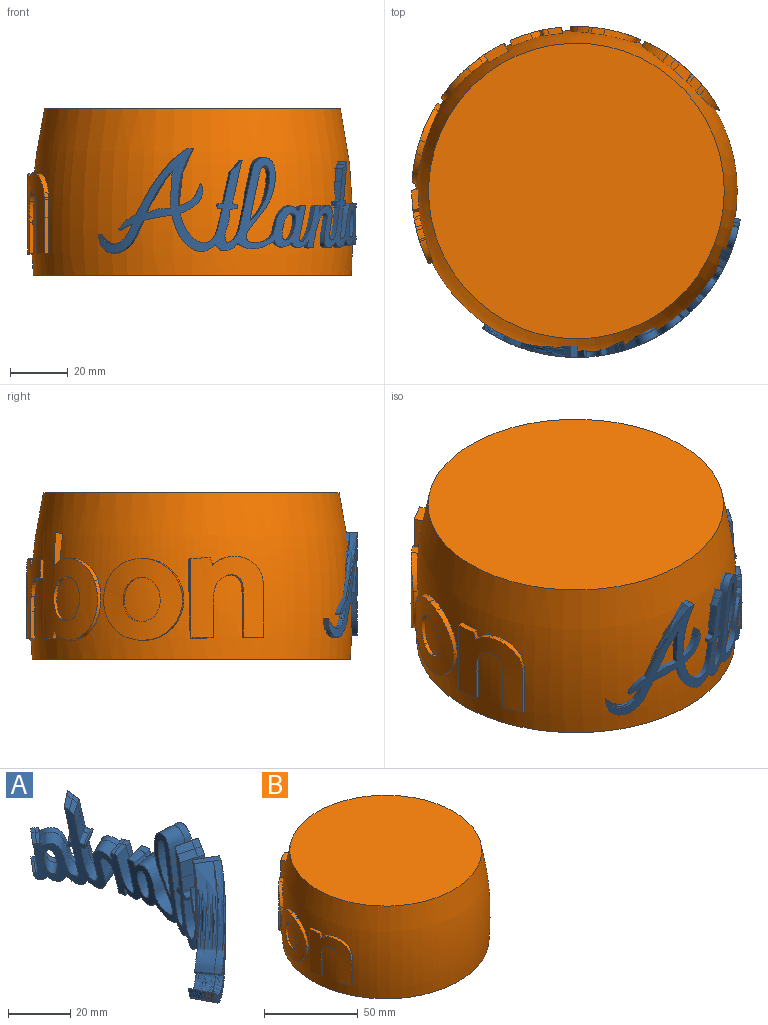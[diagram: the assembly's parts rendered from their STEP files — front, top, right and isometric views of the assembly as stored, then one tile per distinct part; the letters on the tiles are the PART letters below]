
ASSEMBLY  parts=2 mates=1
PART A: 143 faces, bbox 37x96.3x36.3 mm
  f0: bspline ~14.65x13.65mm, area 59.4mm2, adj f1,f70,f71,f133
  f1: bspline ~2.82x2.61mm, area 3.4mm2, adj f0,f2,f71,f132
  f2: bspline ~2.21x1.78mm, area 3.6mm2, adj f1,f3,f71,f131
  f3: bspline ~12.78x11.38mm, area 50.7mm2, adj f2,f4,f71,f130
  f4: bspline ~2.76x1.98mm, area 3.5mm2, adj f3,f5,f71,f129
  f5: bspline ~2.54x1.41mm, area 2mm2, adj f4,f6,f71,f128
  f6: bspline ~19.2x6.49mm, area 51.9mm2, adj f5,f7,f71,f127
  f7: bspline ~2.59x1.72mm, area 4.8mm2, adj f6,f8,f71,f126
  f8: bspline ~2.54x0.68mm, area 2.1mm2, adj f7,f9,f71,f125
  f9: bspline ~6.09x2.81mm, area 17mm2, adj f8,f10,f71,f124
  f10: bspline ~2.59x0.91mm, area 2.1mm2, adj f9,f11,f71,f123
  f11: bspline ~2.58x0.74mm, area 2mm2, adj f10,f12,f71,f122
  f12: bspline ~6.59x3.58mm, area 17.9mm2, adj f11,f13,f71,f121
  f13: bspline ~2.64x1.3mm, area 2.4mm2, adj f12,f14,f71,f120
  f14: bspline ~2.52x1.24mm, area 3.2mm2, adj f13,f15,f71,f119
  f15: bspline ~14.26x12.03mm, area 89.4mm2, adj f14,f16,f71,f118
  f16: bspline ~2.75x2.16mm, area 3.4mm2, adj f15,f17,f71,f117
  f17: bspline ~2.35x1.48mm, area 1.4mm2, adj f16,f18,f71,f116
  f18: bspline ~12.65x10.28mm, area 40.6mm2, adj f17,f19,f71,f115
  f19: bspline ~2.38x2.34mm, area 2.6mm2, adj f18,f20,f71,f114
  f20: bspline ~2.05x2.02mm, area 1.3mm2, adj f19,f21,f71,f113
  f21: bspline ~5.29x5.16mm, area 15.6mm2, adj f20,f22,f71,f112
  f22: bspline ~2.02x1.74mm, area 1.6mm2, adj f21,f23,f71,f111
  f23: bspline ~2.48x2.3mm, area 2.2mm2, adj f22,f24,f71,f110
  f24: bspline ~6.09x2.51mm, area 17.5mm2, adj f23,f25,f71,f109
  f25: bspline ~5.23x2.82mm, area 16.8mm2, adj f24,f26,f71,f108
  f26: bspline ~2.71x2.62mm, area 3.1mm2, adj f25,f27,f71,f107
  f27: bspline ~1.96x1.83mm, area 1.7mm2, adj f26,f28,f71,f106
  f28: bspline ~12.6x12.17mm, area 82.4mm2, adj f27,f29,f71,f105
  f29: bspline ~2.24x1.68mm, area 3.2mm2, adj f28,f30,f71,f104
  f30: bspline ~2.69x2.35mm, area 2.7mm2, adj f29,f31,f71,f103
  f31: bspline ~2.65x2.33mm, area 8.2mm2, adj f30,f32,f71,f102
  f32: bspline ~2.49x2.07mm, area 1.8mm2, adj f31,f33,f71,f101
  f33: bspline ~2.13x1.55mm, area 1.8mm2, adj f32,f34,f71,f100
  f34: bspline ~13.08x3.66mm, area 39.6mm2, adj f33,f35,f71,f99
  f35: bspline ~3.08x2.89mm, area 5.6mm2, adj f34,f36,f71,f98
  f36: bspline ~4.43x2.6mm, area 11.5mm2, adj f35,f37,f71,f97
  f37: bspline ~6.86x3.93mm, area 21.4mm2, adj f36,f38,f71,f96
  f38: bspline ~2.53x1.85mm, area 1.7mm2, adj f37,f39,f71,f95
  f39: bspline ~2.27x1.37mm, area 2mm2, adj f38,f40,f71,f94
  f40: bspline ~2.26x1.38mm, area 2mm2, adj f39,f41,f71,f93
  f41: bspline ~2.61x2.01mm, area 2.1mm2, adj f40,f42,f71,f92
  f42: bspline ~2.61x2.03mm, area 2.1mm2, adj f41,f43,f71,f91
  f43: bspline ~2.2x1.4mm, area 1.5mm2, adj f42,f44,f71,f90
  f44: bspline ~11.97x11.12mm, area 79.3mm2, adj f43,f45,f71,f89
  f45: bspline ~2.7x1.72mm, area 3mm2, adj f44,f46,f71,f88
  f46: bspline ~2.49x1.16mm, area 3mm2, adj f45,f47,f71,f87
  f47: bspline ~2.48x1.16mm, area 3mm2, adj f46,f48,f71,f86
  f48: bspline ~2.81x2.02mm, area 3.2mm2, adj f47,f49,f71,f85
  f49: bspline ~37.31x29.56mm, area 373.9mm2, adj f48,f50,f71,f84
  f50: bspline ~2.48x0.79mm, area 2mm2, adj f49,f51,f71,f83
  f51: bspline ~2.68x1.5mm, area 2.2mm2, adj f50,f52,f71,f82
  f52: bspline ~15.2x4.03mm, area 55.8mm2, adj f51,f53,f71,f81
  f53: bspline ~2.98x2.58mm, area 7.2mm2, adj f52,f54,f71,f80
  f54: bspline ~5.4x2.79mm, area 14.1mm2, adj f53,f55,f71,f79
  f55: bspline ~7.41x4.16mm, area 25.7mm2, adj f54,f56,f71,f78
  f56: bspline ~2.65x1.62mm, area 2mm2, adj f55,f57,f71,f137
  f57: bspline ~2.43x0.99mm, area 1.5mm2, adj f56,f58,f71,f136
  f58: bspline ~32.61x14.33mm, area 187.1mm2, adj f57,f59,f71,f135
  f59: plane 8.79x6.55mm, normal (0,0,1), area 20.3mm2, adj f58,f70,f71,f134,f135,f142
  f60: bspline ~2.12x1.67mm, area 3.8mm2, adj f61,f69,f71,f141
  f61: bspline ~13.05x8.19mm, area 58.6mm2, adj f60,f62,f71,f74
  f62: bspline ~10.63x6.8mm, area 32.3mm2, adj f61,f69,f71,f73
  f63: bspline ~8.79x5.08mm, area 29.7mm2, adj f68,f71,f140
  f64: bspline ~18.49x7.44mm, area 53.5mm2, adj f67,f71,f139
  f65: bspline ~8.97x5.3mm, area 30.4mm2, adj f66,f71,f138
  f66: bspline ~9.16x4.93mm, area 30.1mm2, adj f65,f71,f77
  f67: bspline ~18.74x6.61mm, area 54.1mm2, adj f64,f71,f76
  f68: bspline ~9.01x4.9mm, area 29.7mm2, adj f63,f71,f75
  f69: bspline ~2.55x2.26mm, area 3.3mm2, adj f60,f62,f71,f72
  f70: bspline ~36.35x25.2mm, area 167.7mm2, adj f0,f59,f71,f134
  f71: cylinder r=57.69mm len=96.33mm, axis (0,0,-1), area 1117mm2, adj f0,f1,f2,f3,f4,f5,f6,f7
  f72: bspline ~5.53x4.53mm, area 8.1mm2, adj f69,f73,f141,f142
  f73: bspline ~10.63x8.93mm, area 78.9mm2, adj f62,f72,f74,f142
  f74: bspline ~13.05x10.21mm, area 145.4mm2, adj f61,f73,f141,f142
  f75: bspline ~9.01x7.37mm, area 72.6mm2, adj f68,f140,f142
  f76: bspline ~18.74x7.06mm, area 134.8mm2, adj f67,f139,f142
  f77: bspline ~9.16x6.69mm, area 73.7mm2, adj f66,f138,f142
  f78: bspline ~7.41x7.07mm, area 59.1mm2, adj f55,f79,f137,f142
  f79: bspline ~6.39x5.4mm, area 35mm2, adj f54,f78,f80,f142
  f80: bspline ~6.6x3.49mm, area 17.5mm2, adj f53,f79,f81,f142
  f81: bspline ~15.19x6.89mm, area 109.3mm2, adj f52,f80,f82,f142
  f82: bspline ~6.34x2.43mm, area 5.1mm2, adj f51,f81,f83,f142
  f83: bspline ~6.17x1.71mm, area 5.1mm2, adj f50,f82,f84,f142
  f84: bspline ~35.59x29.44mm, area 905.8mm2, adj f49,f83,f85,f142
  f85: bspline ~6.37x3.19mm, area 7.3mm2, adj f48,f84,f86,f142
  f86: bspline ~6.06x2.39mm, area 7.5mm2, adj f47,f85,f87,f142
  f87: bspline ~6.07x2.37mm, area 7.5mm2, adj f46,f86,f88,f142
  f88: bspline ~6.26x2.95mm, area 7.2mm2, adj f45,f87,f89,f142
  f89: bspline ~11.99x11.96mm, area 197.6mm2, adj f44,f88,f90,f142
  f90: bspline ~5.44x3.4mm, area 3.8mm2, adj f43,f89,f91,f142
  f91: bspline ~5.83x3.96mm, area 4.9mm2, adj f42,f90,f92,f142
  f92: bspline ~5.87x3.88mm, area 4.9mm2, adj f41,f91,f93,f142
  f93: bspline ~5.56x3.27mm, area 4.9mm2, adj f40,f92,f94,f142
  f94: bspline ~5.57x3.26mm, area 4.9mm2, adj f39,f93,f95,f142
  f95: bspline ~5.8x3.72mm, area 3.9mm2, adj f38,f94,f96,f142
  f96: bspline ~6.87x6.86mm, area 52.5mm2, adj f37,f95,f97,f142
  f97: bspline ~5.72x4.43mm, area 28.6mm2, adj f36,f96,f98,f142
  f98: bspline ~6.11x4.98mm, area 13.3mm2, adj f35,f97,f99,f142
  f99: bspline ~13.08x6.55mm, area 111.5mm2, adj f34,f98,f100,f142
  f100: bspline ~5.23x3.75mm, area 4.5mm2, adj f33,f99,f101,f142
  f101: bspline ~5.55x4.24mm, area 4.2mm2, adj f32,f100,f102,f142
  f102: bspline ~5.66x4.54mm, area 19.9mm2, adj f31,f101,f103,f142
  f103: bspline ~5.75x4.49mm, area 6.3mm2, adj f30,f102,f104,f142
  f104: bspline ~5.36x3.83mm, area 8mm2, adj f29,f103,f105,f142
  f105: bspline ~14.16x13.29mm, area 200.8mm2, adj f28,f104,f106,f142
  f106: bspline ~4.75x4.41mm, area 4.2mm2, adj f27,f105,f107,f142
  f107: bspline ~5.47x5.1mm, area 7.2mm2, adj f26,f106,f108,f142
  f108: bspline ~5.63x5.23mm, area 41.3mm2, adj f25,f107,f109,f142
  f109: bspline ~6.09x5.31mm, area 43.2mm2, adj f24,f108,f110,f142
  f110: bspline ~5.33x4.73mm, area 5mm2, adj f23,f109,f111,f142
  f111: bspline ~4.93x4.2mm, area 3.9mm2, adj f22,f110,f112,f142
  f112: bspline ~7.7x7.6mm, area 37.1mm2, adj f21,f111,f113,f142
  f113: bspline ~4.74x4.68mm, area 3.2mm2, adj f20,f112,f114,f142
  f114: bspline ~5.08x4.94mm, area 6.1mm2, adj f19,f113,f115,f142
  f115: bspline ~14.02x12.67mm, area 95.1mm2, adj f18,f114,f116,f142
  f116: bspline ~5.66x3.33mm, area 3.5mm2, adj f17,f115,f117,f142
  f117: bspline ~6.05x3.91mm, area 8mm2, adj f16,f116,f118,f142
  f118: bspline ~14.55x12.02mm, area 223.3mm2, adj f15,f117,f119,f142
  f119: bspline ~6.22x1.73mm, area 8mm2, adj f14,f118,f120,f142
  f120: bspline ~6.33x2.14mm, area 5.8mm2, adj f13,f119,f121,f142
  f121: bspline ~7.24x6.77mm, area 41.9mm2, adj f12,f120,f122,f142
  f122: bspline ~6.36x1.15mm, area 5mm2, adj f11,f121,f123,f142
  f123: bspline ~6.38x1.26mm, area 5mm2, adj f10,f122,f124,f142
  f124: bspline ~6.59x5.82mm, area 40.1mm2, adj f9,f123,f125,f142
  f125: bspline ~6.35x0.68mm, area 5mm2, adj f8,f124,f126,f142
  f126: bspline ~6.39x1.7mm, area 11.3mm2, adj f7,f125,f127,f142
  f127: bspline ~18.52x9.84mm, area 129.2mm2, adj f6,f126,f128,f142
  f128: bspline ~6.05x2.82mm, area 4.8mm2, adj f5,f127,f129,f142
  f129: bspline ~6.23x3.39mm, area 8.3mm2, adj f4,f128,f130,f142
  f130: bspline ~13.78x11.65mm, area 121.7mm2, adj f3,f129,f131,f142
  f131: bspline ~5.22x4.07mm, area 9.1mm2, adj f2,f130,f132,f142
  f132: bspline ~5.75x4.88mm, area 7.9mm2, adj f1,f131,f133,f142
  f133: bspline ~16.16x15.5mm, area 144.2mm2, adj f0,f132,f134,f142
  f134: bspline ~36.35x25.76mm, area 403.7mm2, adj f59,f70,f133,f142
  f135: bspline ~32.61x15.04mm, area 456.2mm2, adj f58,f59,f136,f142
  f136: bspline ~6.01x2.29mm, area 3.7mm2, adj f57,f135,f137,f142
  f137: bspline ~6.2x2.89mm, area 4.6mm2, adj f56,f78,f136,f142
  f138: bspline ~8.98x6.77mm, area 73.9mm2, adj f65,f77,f142
  f139: bspline ~18.48x7.29mm, area 131.7mm2, adj f64,f76,f142
  f140: bspline ~8.79x7.52mm, area 72.4mm2, adj f63,f75,f142
  f141: bspline ~5.14x3.97mm, area 9.5mm2, adj f60,f72,f74,f142
  f142: cylinder r=48.8mm len=81.51mm, axis (0,0,1), area 636mm2, adj f59,f72,f73,f74,f75,f76,f77,f78
PART B: 163 faces, bbox 114.9x114.1x85.4 mm
  f0: revolved ~111.7x111.7mm, area 16699mm2, adj f1,f3,f4,f5,f6,f7,f8,f9
  f1: extruded ~5.58x2.8mm, area 8.1mm2, adj f0,f2,f3,f26
  f2: cylinder r=57.15mm len=28.37mm, axis (0,0,-1), area 485.4mm2, adj f1,f3,f4,f5,f6,f7,f8,f9
  f3: extruded ~8.74x5.34mm, area 16.4mm2, adj f0,f1,f2,f4
  f4: extruded ~5.71x2.17mm, area 9mm2, adj f0,f2,f3,f5
  f5: extruded ~1.47x0.91mm, area 1.1mm2, adj f0,f2,f4,f6
  f6: plane 14.32x1.42mm, normal (-0.31,0.95,0), area 19.1mm2, adj f0,f2,f5,f7
  f7: plane 7.54x4.35mm, normal (-0.1,-0.03,-0.99), area 11.4mm2, adj f0,f2,f6,f8
  f8: plane 12.57x1.43mm, normal (0.31,-0.95,0), area 16.9mm2, adj f0,f2,f7,f9
  f9: extruded ~6.58x2.56mm, area 9.5mm2, adj f0,f2,f8,f10
  f10: extruded ~1.52x0.52mm, area 0.1mm2, adj f0,f2,f9,f11
  f11: extruded ~1.63x0.87mm, area 1.1mm2, adj f0,f2,f10,f12
  f12: extruded ~1.79x1.75mm, area 2.7mm2, adj f0,f2,f11,f13
  f13: extruded ~8.44x6.96mm, area 21.2mm2, adj f0,f2,f12,f14
  f14: extruded ~2.37x1.44mm, area 1.8mm2, adj f0,f2,f13,f15
  f15: extruded ~3.77x3.27mm, area 7.3mm2, adj f0,f2,f14,f16
  f16: extruded ~2.68x1.93mm, area 2.9mm2, adj f0,f2,f15,f17
  f17: extruded ~3.29x3.08mm, area 5.8mm2, adj f0,f2,f16,f18
  f18: extruded ~2.56x1.59mm, area 2.4mm2, adj f0,f2,f17,f19
  f19: extruded ~2.99x2.34mm, area 4.4mm2, adj f0,f2,f18,f20
  f20: extruded ~2.76x2.18mm, area 5.7mm2, adj f0,f2,f19,f21
  f21: plane 7.62x2.57mm, normal (0.1,0.03,0.99), area 15.3mm2, adj f0,f2,f20,f22
  f22: plane 27.7x2.22mm, normal (-0.31,0.95,0), area 38.8mm2, adj f0,f2,f21,f23,f24
  f23: plane 9.78x4.3mm, normal (0.94,0.31,-0.11), area 18.2mm2, adj f0,f22,f24
  f24: plane 8.11x2mm, normal (-0.1,-0.03,-0.99), area 9.5mm2, adj f0,f2,f22,f23,f25
  f25: plane 10.98x1.44mm, normal (0.31,-0.95,0), area 14.9mm2, adj f0,f2,f24,f26
  f26: extruded ~2.05x1.65mm, area 2.6mm2, adj f0,f1,f2,f25
  f27: extruded ~5.3x1.79mm, area 7.4mm2, adj f0,f28,f34,f47
  f28: cylinder r=57.15mm len=28.42mm, axis (0,0,-1), area 487.7mm2, adj f27,f29,f31,f32,f33,f34,f35,f36
  f29: extruded ~2.78x2.36mm, area 4mm2, adj f28,f30,f31,f33
  f30: revolved ~15.08x12.94mm, area 162.4mm2, adj f29,f31,f32,f33
  f31: extruded ~13.83x6.18mm, area 26.1mm2, adj f28,f29,f30,f32
  f32: extruded ~5.68x3.05mm, area 7.7mm2, adj f28,f30,f31,f33
  f33: extruded ~15.03x5.69mm, area 30mm2, adj f28,f29,f30,f32
  f34: extruded ~7.88x7.36mm, area 15.1mm2, adj f0,f27,f28,f35
  f35: extruded ~4.55x2.99mm, area 6.6mm2, adj f0,f28,f34,f36
  f36: extruded ~4.74x2.86mm, area 6.8mm2, adj f0,f28,f35,f37
  f37: extruded ~1.51x0.63mm, area 0.3mm2, adj f0,f28,f36,f38
  f38: extruded ~1.98x1.92mm, area 2.3mm2, adj f0,f28,f37,f39
  f39: extruded ~5x3.21mm, area 7.5mm2, adj f0,f28,f38,f40
  f40: extruded ~4.91x4.89mm, area 9.3mm2, adj f0,f28,f39,f41
  f41: extruded ~7.63x2.41mm, area 11mm2, adj f0,f28,f40,f42
  f42: extruded ~1.35x0.44mm, area 0.1mm2, adj f0,f28,f41,f43
  f43: extruded ~13.12x10.53mm, area 31.4mm2, adj f0,f28,f42,f44
  f44: extruded ~5.34x3.77mm, area 10.8mm2, adj f0,f28,f43,f45
  f45: extruded ~12.11x6.48mm, area 27.4mm2, adj f0,f28,f44,f46
  f46: extruded ~6.84x2.82mm, area 11.4mm2, adj f0,f28,f45,f47
  f47: extruded ~1.37x0.7mm, area 1mm2, adj f0,f27,f28,f46
  f48: plane 6.76x4.52mm, normal (-0.05,0.08,-1), area 10.1mm2, adj f0,f49,f56,f67
  f49: cylinder r=57.15mm len=37.35mm, axis (0,0,-1), area 628.3mm2, adj f48,f50,f52,f53,f54,f55,f56,f57
  f50: extruded ~13.67x5.62mm, area 24.5mm2, adj f49,f51,f52,f55
  f51: revolved ~15.16x10.77mm, area 165.3mm2, adj f50,f52,f53,f54,f55
  f52: extruded ~5.78x4.92mm, area 9.6mm2, adj f49,f50,f51,f53
  f53: extruded ~4.84x4.54mm, area 9.6mm2, adj f49,f51,f52,f54
  f54: extruded ~12.11x5.64mm, area 20.3mm2, adj f49,f51,f53,f55
  f55: extruded ~4.02x3.51mm, area 5.1mm2, adj f49,f50,f51,f54
  f56: extruded ~2.68x2.12mm, area 3.9mm2, adj f0,f48,f49,f57
  f57: extruded ~2.57x2.28mm, area 3.5mm2, adj f0,f49,f56,f58
  f58: extruded ~7.8x6.33mm, area 12.5mm2, adj f0,f49,f57,f59
  f59: extruded ~1.57x1.35mm, area 0.8mm2, adj f0,f49,f58,f60
  f60: extruded ~3.39x3.25mm, area 4.4mm2, adj f0,f49,f59,f61
  f61: extruded ~20.3x8.65mm, area 35.6mm2, adj f0,f49,f60,f62
  f62: extruded ~13.11x10.53mm, area 29.8mm2, adj f0,f49,f61,f63
  f63: extruded ~5.59x5.12mm, area 11.9mm2, adj f0,f49,f62,f64
  f64: extruded ~3.08x2.88mm, area 5.1mm2, adj f0,f49,f63,f65
  f65: plane 11.48x2.7mm, normal (-0.81,-0.59,-0.01), area 29.1mm2, adj f0,f49,f64,f66
  f66: plane 8.72x6.6mm, normal (0.05,-0.08,1), area 25.6mm2, adj f0,f49,f65,f67
  f67: plane 36.86x2.85mm, normal (0.81,0.59,0.01), area 67.6mm2, adj f0,f48,f49,f66
  f68: extruded ~1.49x0.68mm, area 1mm2, adj f0,f69,f76,f99
  f69: cylinder r=57.15mm len=28.42mm, axis (0,0,-1), area 512.6mm2, adj f68,f70,f72,f73,f74,f75,f76,f77
  f70: extruded ~8.39x4.7mm, area 12.3mm2, adj f69,f71,f72,f75
  f71: revolved ~9.22x6.16mm, area 47.1mm2, adj f70,f72,f73,f74,f75
  f72: extruded ~3.35x1.34mm, area 4.5mm2, adj f69,f70,f71,f73
  f73: extruded ~4.86x3.37mm, area 5.9mm2, adj f69,f71,f72,f74
  f74: extruded ~2.74x2.23mm, area 3.2mm2, adj f69,f71,f73,f75
  f75: extruded ~4.88x2.77mm, area 8.3mm2, adj f69,f70,f71,f74
  f76: plane 7.39x3.73mm, normal (0,0.02,-1), area 11.1mm2, adj f0,f68,f69,f77
  f77: extruded ~7.85x4.67mm, area 14.6mm2, adj f0,f69,f76,f78
  f78: extruded ~3.29x2.06mm, area 5.6mm2, adj f0,f69,f77,f79
  f79: extruded ~7.32x4.52mm, area 10.3mm2, adj f0,f69,f78,f80
  f80: extruded ~5.55x3.18mm, area 8mm2, adj f0,f69,f79,f81
  f81: extruded ~13.89x4.99mm, area 23.6mm2, adj f0,f69,f80,f82
  f82: extruded ~3.78x2.58mm, area 5.8mm2, adj f0,f69,f81,f83
  f83: extruded ~2.62x2.27mm, area 3.5mm2, adj f0,f69,f82,f84
  f84: plane 1.49x0.6mm, normal (0,-0.02,1), area 0.2mm2, adj f0,f69,f83,f85
  f85: extruded ~4.03x2.91mm, area 5.6mm2, adj f0,f69,f84,f86
  f86: extruded ~1.54x0.65mm, area 0.3mm2, adj f0,f69,f85,f87
  f87: extruded ~5.51x3.65mm, area 8.7mm2, adj f0,f69,f86,f88
  f88: extruded ~2.15x2.1mm, area 3.5mm2, adj f0,f69,f87,f89
  f89: extruded ~2.5x2.36mm, area 2.9mm2, adj f0,f69,f88,f90
  f90: plane 5.15x1.57mm, normal (0,0.02,-1), area 7mm2, adj f0,f69,f89,f91
  f91: plane 15.38x1.54mm, normal (-0.95,0.31,0.01), area 22.1mm2, adj f0,f69,f90,f92
  f92: extruded ~1.44x0.47mm, area 0.6mm2, adj f0,f69,f91,f93
  f93: extruded ~8.66x3.24mm, area 16mm2, adj f0,f69,f92,f94
  f94: extruded ~4.54x4.17mm, area 9.7mm2, adj f0,f69,f93,f95
  f95: extruded ~2.67x1.79mm, area 2.5mm2, adj f0,f69,f94,f96
  f96: extruded ~5.08x4.22mm, area 9.8mm2, adj f0,f69,f95,f97
  f97: extruded ~11.12x5.7mm, area 25.3mm2, adj f0,f69,f96,f98
  f98: extruded ~3.78x1.9mm, area 6.5mm2, adj f0,f69,f97,f99
  f99: extruded ~1.48x0.48mm, area 0.1mm2, adj f0,f68,f69,f98
  f100: extruded ~8.63x7.93mm, area 25.7mm2, adj f0,f101,f106,f107,f137
  f101: cylinder r=57.15mm len=38.3mm, axis (0,0,-1), area 628.5mm2, adj f100,f102,f103,f104,f105,f106,f108,f109
  f102: extruded ~2.37x1.25mm, area 1.8mm2, adj f101,f103,f107,f108
  f103: extruded ~2.66x0.85mm, area 1.3mm2, adj f101,f102,f104,f107
  f104: extruded ~5.87x0.55mm, area 2mm2, adj f101,f103,f105,f107
  f105: extruded ~0.65x0.31mm, area 0.2mm2, adj f101,f104,f106,f107
  f106: extruded ~5.08x1.74mm, area 3.6mm2, adj f100,f101,f105,f107
  f107: plane 26.02x5.36mm, normal (-0.59,-0.81,-0.02), area 61.4mm2, adj f0,f100,f102,f103,f104,f105,f106,f108
  f108: extruded ~8.16x7.76mm, area 15.7mm2, adj f0,f101,f102,f107,f109
  f109: extruded ~5.02x4.62mm, area 7.2mm2, adj f0,f101,f108,f110
  f110: extruded ~3.35x3.19mm, area 4.3mm2, adj f0,f101,f109,f111
  f111: extruded ~4.83x4.26mm, area 7mm2, adj f0,f101,f110,f112
  f112: extruded ~1.43x1.16mm, area 0.5mm2, adj f0,f101,f111,f113
  f113: extruded ~2.56x2.47mm, area 3mm2, adj f0,f101,f112,f114
  f114: extruded ~4.21x3.61mm, area 6.5mm2, adj f0,f101,f113,f115
  f115: extruded ~11.2x8.27mm, area 20.2mm2, adj f0,f101,f114,f116
  f116: plane 6.05x3.82mm, normal (0,-0.02,1), area 7.9mm2, adj f0,f101,f115,f117
  f117: extruded ~2.75x2.57mm, area 3.1mm2, adj f0,f101,f116,f118
  f118: extruded ~1.39x1.21mm, area 1mm2, adj f0,f101,f117,f119
  f119: extruded ~1.19x0.96mm, area 0.6mm2, adj f0,f101,f118,f120
  f120: extruded ~1.37x1.21mm, area 1.3mm2, adj f0,f101,f119,f121
  f121: extruded ~1.38x1.24mm, area 1.4mm2, adj f0,f101,f120,f122
  f122: extruded ~5.3x4.36mm, area 8.1mm2, adj f0,f101,f121,f123
  f123: extruded ~8.24x7.01mm, area 12.1mm2, adj f0,f101,f122,f124
  f124: extruded ~19.15x5.38mm, area 36.4mm2, adj f0,f101,f123,f125
  f125: extruded ~11.99x10.05mm, area 30.3mm2, adj f0,f101,f124,f126
  f126: extruded ~1.83x1.36mm, area 0.2mm2, adj f0,f101,f125,f127
  f127: extruded ~1.97x1.54mm, area 1mm2, adj f0,f101,f126,f128
  f128: extruded ~2.62x2.61mm, area 6.1mm2, adj f0,f101,f127,f129
  f129: plane 8.56x5.68mm, normal (0,0.02,-1), area 16.5mm2, adj f0,f101,f128,f130
  f130: extruded ~11.04x8.93mm, area 37.4mm2, adj f0,f101,f129,f131
  f131: extruded ~4.57x4.51mm, area 11mm2, adj f0,f101,f130,f132
  f132: extruded ~3.97x3.64mm, area 6.9mm2, adj f0,f101,f131,f133
  f133: extruded ~6.93x6.56mm, area 19.4mm2, adj f0,f101,f132,f134
  f134: extruded ~2.93x2.22mm, area 0.9mm2, adj f0,f101,f133,f135
  f135: extruded ~3.78x3.3mm, area 4.9mm2, adj f0,f101,f134,f136
  f136: extruded ~5.48x5.44mm, area 13.2mm2, adj f0,f101,f135,f137
  f137: extruded ~3.99x3.6mm, area 6.6mm2, adj f0,f100,f101,f136
  f138: plane 8.23x2.71mm, normal (0,0.02,-1), area 11.8mm2, adj f0,f139,f140,f150
  f139: cylinder r=57.15mm len=27.54mm, axis (0,0,-1), area 290.5mm2, adj f138,f140,f141,f142,f143,f144,f145,f146
  f140: plane 9.53x1.44mm, normal (-0.95,-0.31,-0.01), area 13mm2, adj f0,f138,f139,f141
  f141: extruded ~5.25x1.51mm, area 7mm2, adj f0,f139,f140,f142
  f142: extruded ~5.4x3.44mm, area 9.7mm2, adj f0,f139,f141,f143
  f143: extruded ~7.36x4.04mm, area 12mm2, adj f0,f139,f142,f144
  f144: plane 6.53x2.11mm, normal (-0.95,-0.31,-0.01), area 12.4mm2, adj f0,f139,f143,f145
  f145: extruded ~7.82x4.62mm, area 16.3mm2, adj f0,f139,f144,f146
  f146: extruded ~3.69x3.13mm, area 8mm2, adj f0,f139,f145,f147
  f147: extruded ~2.42x2.39mm, area 5.5mm2, adj f0,f139,f146,f148
  f148: extruded ~2.87x2.48mm, area 4.1mm2, adj f0,f139,f147,f149
  f149: plane 5.32x2.75mm, normal (0,-0.02,1), area 10.2mm2, adj f0,f139,f148,f150
  f150: plane 27.57x2.18mm, normal (0.95,0.31,0.01), area 43mm2, adj f0,f138,f139,f149
  f151: bspline ~28.63x5.68mm, area 0mm2, adj f0,f162
  f152: bspline ~28.62x5.7mm, area 0mm2, adj f0,f162
  f153: bspline ~28.62x5.47mm, area 0mm2, adj f0,f162
  f154: bspline ~28.62x5.96mm, area 0mm2, adj f0,f162
  f155: bspline ~28.63x5.23mm, area 0mm2, adj f0,f162
  f156: bspline ~28.62x5.68mm, area 0mm2, adj f0,f162
  f157: bspline ~28.63x5.71mm, area 0mm2, adj f0,f162
  f158: bspline ~28.63x5.47mm, area 0mm2, adj f0,f162
  f159: bspline ~28.62x5.98mm, area 0mm2, adj f0,f162
  f160: plane 102.65x102.65mm, normal (0,0,1), area 8275.7mm2, adj f0
  f161: bspline ~28.62x5.23mm, area 0mm2, adj f0,f162
  f162: plane 110.42x110.42mm, normal (0,0,-1), area 9568.6mm2, adj f0,f151,f152,f153,f154,f155,f156,f157
PLACE A rot(axis=(0,0,-1),59.7deg) t=(0,0,5.94)mm
PLACE B t=(0,0,-171.45)mm
MATE revolute A.f71 <-> B.f2  axis (0,0,1) through (0,0,25.76)mm
